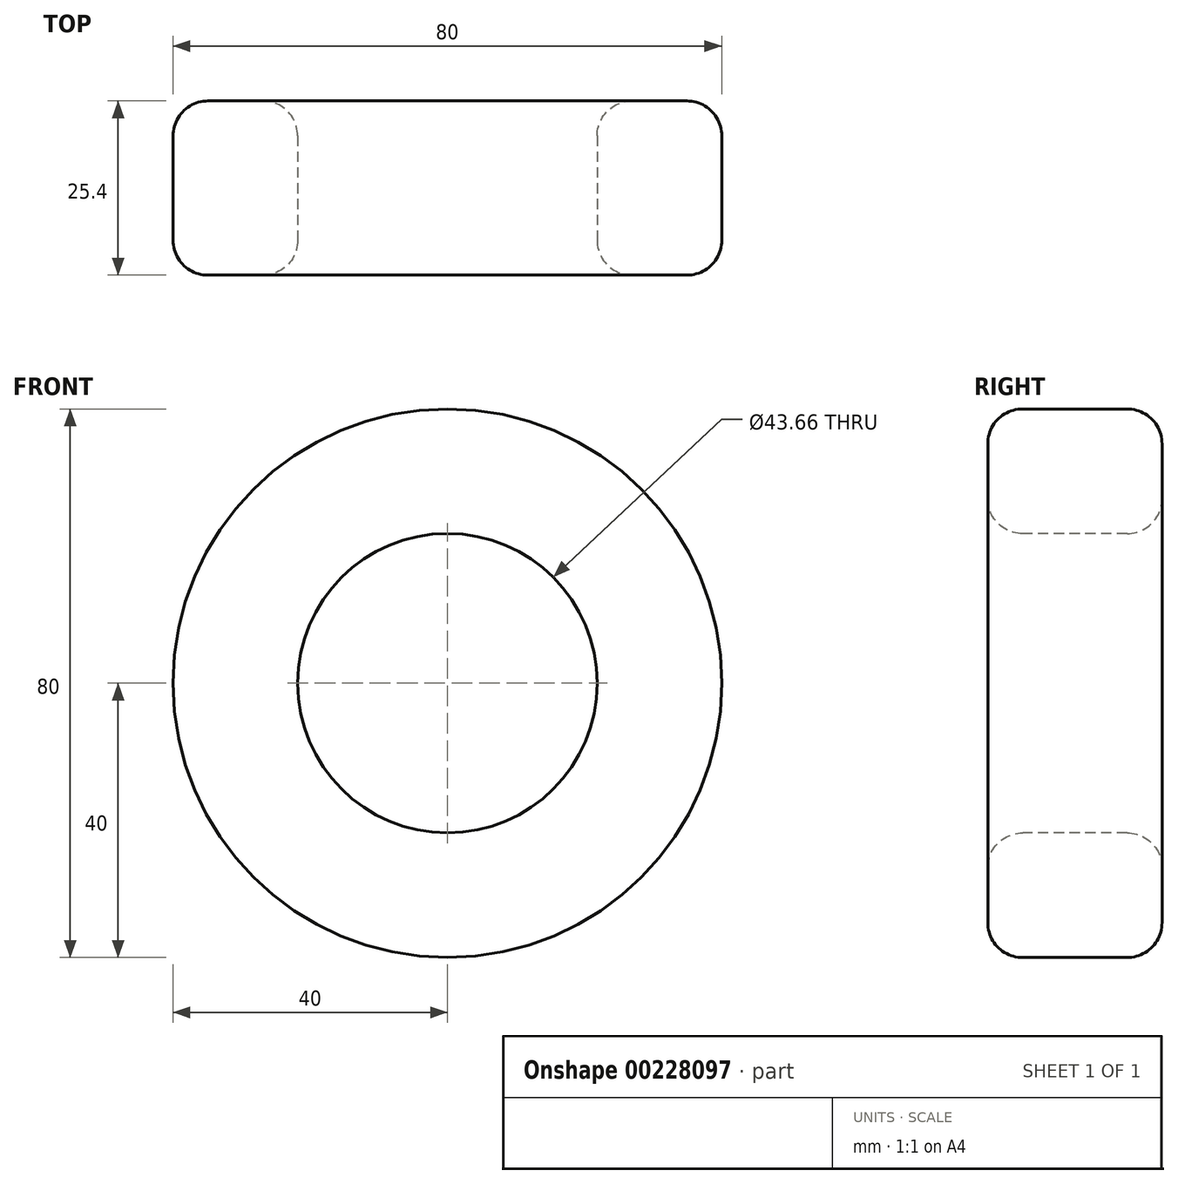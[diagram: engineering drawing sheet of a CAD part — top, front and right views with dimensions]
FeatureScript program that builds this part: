
annotation { "Feature Type Name" : "Feature", "Feature Type Description" : "" }
export const myFeature = defineFeature(function(context is Context, id is Id, definition is map)
    precondition{}
    {
        {
            var Q0;
            Q0=qCreatedBy(makeId("Front.planeOp"),FACE);
            var sketch = newSketch(context, id + "F0", { "sketchPlane" : qUnion([Q0])});
            skCircle(sketch, "E0", {"center": v(0, 0) * mm, "radius": 40 * mm});
            skSolve(sketch);
        }
        {
            var Q0;
            Q0=makeQuery(id+"F0.imprint","IMPRINT",FACE,{"disambiguationData":[TD([[makeQuery(id+"F0.imprint","IMPRINT",EDGE,{"derivedFrom":sQuery(id+"F0.wireOp",EDGE,"E0")}),1.0]])]});
            extrude(context, id + "F1", {"entities" : qUnion([Q0]), "depth" : 25.4 * mm});
        }
        {
            var Q0;
            Q0=makeQuery(id+"F1.opExtrude","CAP_FACE",FACE,{"disambiguationData":[OSD([sQuery(id+"F0.wireOp",EDGE,"E0")])],"isStart":false});
            var sketch = newSketch(context, id + "F2", { "sketchPlane" : qUnion([Q0])});
            skCircle(sketch, "E1", {"center": v(0, 0) * mm, "radius": 21.83 * mm});
            skSolve(sketch);
        }
        {
            var Q0;
            Q0=makeQuery(id+"F2.imprint","IMPRINT",FACE,{"disambiguationData":[TD([[makeQuery(id+"F2.imprint","IMPRINT",EDGE,{"derivedFrom":sQuery(id+"F2.wireOp",EDGE,"E1")}),1.0]])]});
            extrude(context, id + "F3", {"entities" : qUnion([Q0]), "operationType" : NewBodyOperationType.REMOVE, "oppositeDirection" : true, "depth" : 25.4 * mm});
        }
        {
            var Q0;
            Q0=makeQuery(id+"F1.opExtrude","CAP_FACE",FACE,{"disambiguationData":[OSD([sQuery(id+"F0.wireOp",EDGE,"E0")])],"isStart":false});
            fillet(context, id + "F4", {"entities" : qUnion([Q0]), "radius" : 5.08 * mm, "tangentPropagation" : true, "allowEdgeOverflow" : false});
        }
        {
            var Q0;
            Q0=makeQuery(id+"F1.opExtrude","CAP_FACE",FACE,{"disambiguationData":[OSD([sQuery(id+"F0.wireOp",EDGE,"E0")])],"isStart":true});
            fillet(context, id + "F5", {"entities" : qUnion([Q0]), "radius" : 5.08 * mm, "tangentPropagation" : true, "allowEdgeOverflow" : false});
        }
    });
